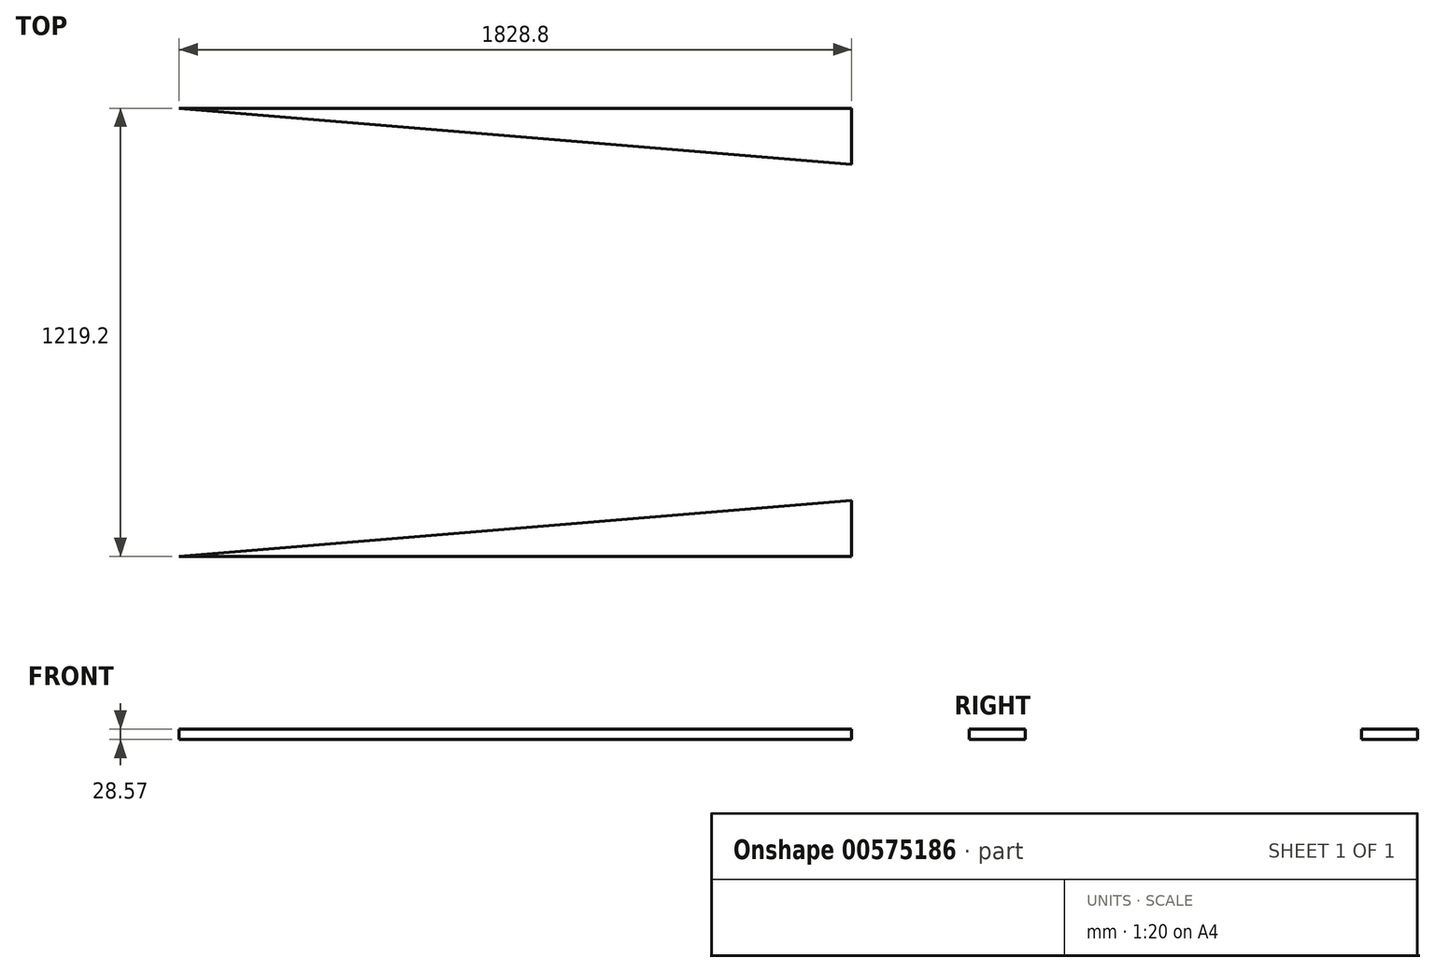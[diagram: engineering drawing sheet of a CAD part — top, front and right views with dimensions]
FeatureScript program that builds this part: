
annotation { "Feature Type Name" : "Feature", "Feature Type Description" : "" }
export const myFeature = defineFeature(function(context is Context, id is Id, definition is map)
    precondition{}
    {
        {
            var Q0;
            Q0=qCreatedBy(makeId("Top.planeOp"),FACE);
            var sketch = newSketch(context, id + "F0", { "sketchPlane" : qUnion([Q0])});
            skLineSegment(sketch, "E0.bottom", {"start": v(914.4, 609.6) * mm, "end": v(-914.4, 609.6) * mm});
            skLineSegment(sketch, "E0.top", {"start": v(914.4, -609.6) * mm, "end": v(-914.4, -609.6) * mm});
            skLineSegment(sketch, "E0.left", {"start": v(914.4, 609.6) * mm, "end": v(914.4, -609.6) * mm});
            skLineSegment(sketch, "E0.right", {"start": v(-914.4, 609.6) * mm, "end": v(-914.4, -609.6) * mm});
            skPoint(sketch, "E0.middle", {"position": v(0, 0) * mm});
            skLineSegment(sketch, "E1", {"start": v(-914.4, 0) * mm, "end": v(-825.5, 0) * mm});
            skPoint(sketch, "E1.endSnap0", {"position": v(-914.4, 0) * mm});
            skCircle(sketch, "E2", {"center": v(-825.5, 0) * mm, "radius": 44.45 * mm});
            skLineSegment(sketch, "E3", {"start": v(914.4, 609.6) * mm, "end": v(914.4, 457.2) * mm});
            skLineSegment(sketch, "E4", {"start": v(914.4, -609.6) * mm, "end": v(914.4, -457.2) * mm});
            skLineSegment(sketch, "E5", {"start": v(-914.4, 609.6) * mm, "end": v(914.4, 457.2) * mm});
            skLineSegment(sketch, "E6", {"start": v(-914.4, -609.6) * mm, "end": v(914.4, -457.2) * mm});
            skLineSegment(sketch, "E7", {"start": v(-914.4, 609.6) * mm, "end": v(-609.6, 609.6) * mm});
            skLineSegment(sketch, "E8", {"start": v(-914.4, -609.6) * mm, "end": v(-609.6, -609.6) * mm});
            skArc(sketch, "E9", {"start": v(914.4, 457.2) * mm, "mid": v(3.8, 579) * mm, "end": v(-914.4, 609.6) * mm});
            skArc(sketch, "E10", {"start": v(-914.4, -609.6) * mm, "mid": v(3.8, -579) * mm, "end": v(914.4, -457.2) * mm});
            skSolve(sketch);
        }
        {
            var Q0;
            Q0=makeQuery(id+"F0.imprint","IMPRINT",FACE,{"disambiguationData":[TD([[makeQuery(id+"F0.imprint","IMPRINT",EDGE,{"derivedFrom":sQuery(id+"F0.wireOp",EDGE,"E0.left")}),-1.0]])]});
            var Q1;
            {var subQ0=sQuery(id+"F0.wireOp",EDGE,"E5");Q1=makeQuery(id+"F0.imprint","IMPRINT",FACE,{"disambiguationData":[TD([[makeQuery(id+"F0.imprint","IMPRINT",EDGE,{"derivedFrom":subQ0}),1.0]])]});}
            var Q2;
            {var subQ0=sQuery(id+"F0.wireOp",EDGE,"E6");Q2=makeQuery(id+"F0.imprint","IMPRINT",FACE,{"disambiguationData":[TD([[makeQuery(id+"F0.imprint","IMPRINT",EDGE,{"derivedFrom":subQ0}),-1.0]])]});}
            extrude(context, id + "F1", {"entities" : qUnion([Q0, Q1, Q2]), "depth" : 28.57 * mm, "offsetDistance" : 25.4 * mm});
        }
    });
